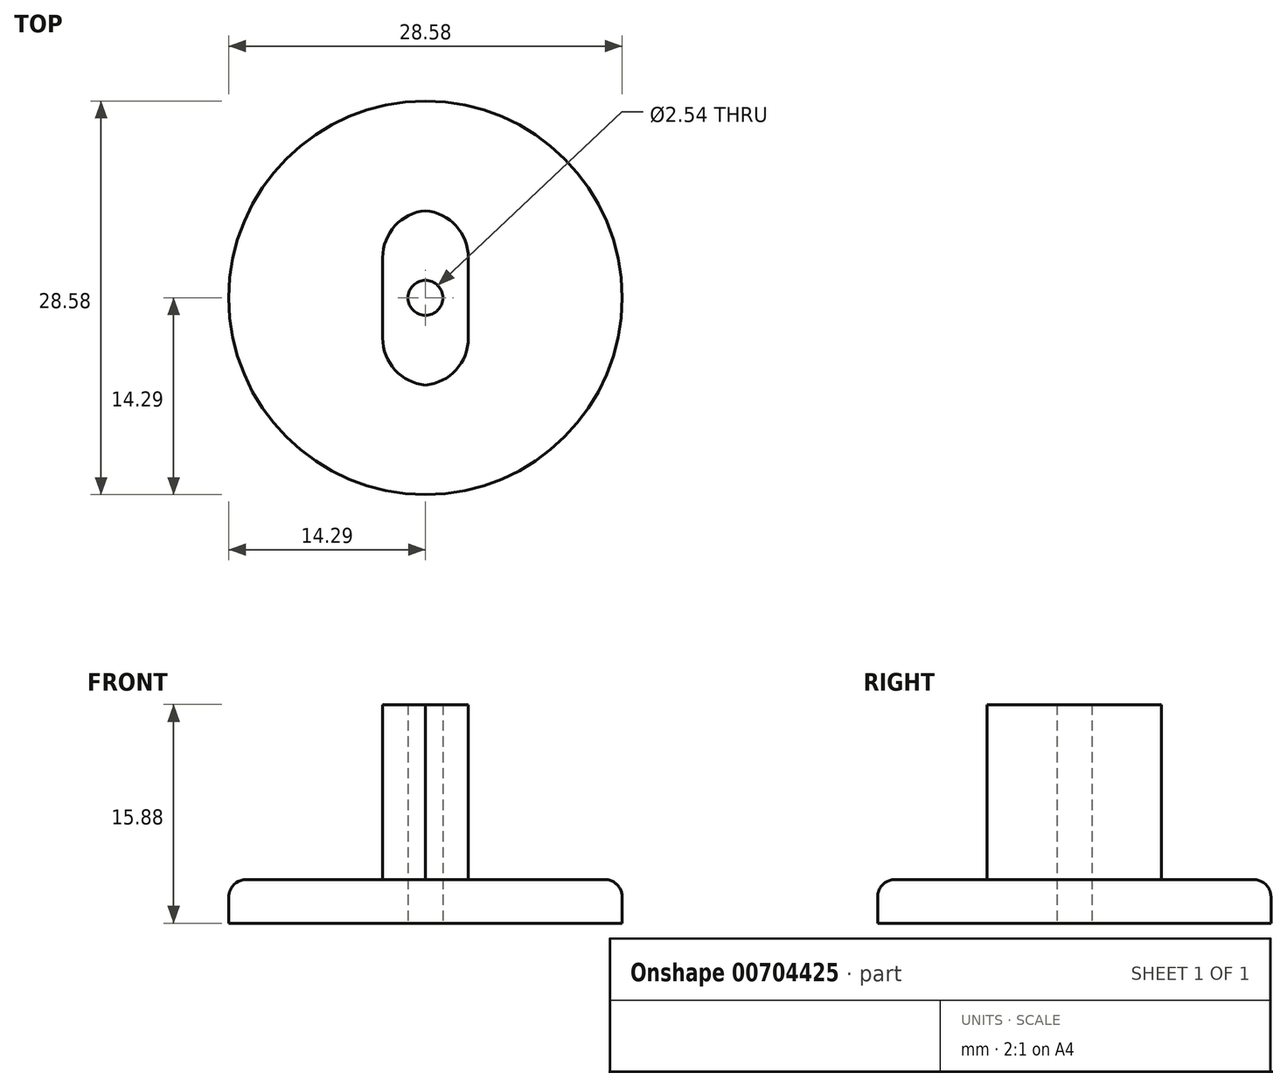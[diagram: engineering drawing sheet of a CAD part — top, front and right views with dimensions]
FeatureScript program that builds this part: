
annotation { "Feature Type Name" : "Feature", "Feature Type Description" : "" }
export const myFeature = defineFeature(function(context is Context, id is Id, definition is map)
    precondition{}
    {
        {
            var Q0;
            Q0=qCreatedBy(makeId("Top.planeOp"),FACE);
            var sketch = newSketch(context, id + "F0", { "sketchPlane" : qUnion([Q0])});
            skCircle(sketch, "E0", {"center": v(0, 0) * mm, "radius": 14.29 * mm});
            skSolve(sketch);
        }
        {
            var Q0;
            Q0 = qSketchRegion(id + "F0", true);
            var Q1;
            Q1 = qSketchRegion(id + "F64pG9NLJwbXjTU_1", true);
            extrude(context, id + "F1", {"entities" : qUnion([Q0, Q1]), "depth" : 3.17 * mm, "offsetDistance" : 25.4 * mm});
        }
        {
            var Q0;
            Q0=makeQuery(id+"F1.opExtrude","CAP_FACE",FACE,{"disambiguationData":[OSD([sQuery(id+"F0.wireOp",EDGE,"E0")])],"isStart":true});
            var sketch = newSketch(context, id + "F2", { "sketchPlane" : qUnion([Q0])});
            skCircle(sketch, "E1", {"center": v(0, 0) * mm, "radius": 0.64 * mm});
            skSolve(sketch);
        }
        {
            var Q0;
            Q0=sQuery(id+"F2.wireOp",VERTEX,"E1.center");
            var Q1;
            Q1=makeQuery(id+"F1.opExtrude","SWEPT_BODY",BODY,{"disambiguationData":[OSD([sQuery(id+"F0.wireOp",EDGE,"E0")])]});
            hole(context, id + "F3", {"style" : HoleStyle.SIMPLE, "endStyle" : HoleEndStyle.THROUGH, "holeDiameter" : 2.54 * mm, "majorDiameter" : 6.35 * mm, "isTappedThrough" : true, "tappedDepth" : 12.7 * mm, "tapClearance" : 3, "locations" : qUnion([Q0]), "scope" : qUnion([Q1])});
        }
        {
            var Q0;
            Q0=makeQuery(id+"F1.opExtrude","CAP_EDGE",EDGE,{"disambiguationData":[OSD([sQuery(id+"F0.wireOp",EDGE,"E0")])],"isStart":false});
            fillet(context, id + "F4", {"entities" : qUnion([Q0]), "radius" : 1.27 * mm, "tangentPropagation" : true, "allowEdgeOverflow" : false});
        }
        {
            var Q0;
            Q0=makeQuery(id+"F1.opExtrude","CAP_FACE",FACE,{"disambiguationData":[OSD([sQuery(id+"F0.wireOp",EDGE,"E0")])],"isStart":false});
            var sketch = newSketch(context, id + "F5", { "sketchPlane" : qUnion([Q0])});
            skLineSegment(sketch, "E2.bottom", {"start": v(3.11, 6.35) * mm, "end": v(-3.11, 6.35) * mm});
            skLineSegment(sketch, "E2.top", {"start": v(3.11, -6.35) * mm, "end": v(-3.11, -6.35) * mm});
            skLineSegment(sketch, "E2.left", {"start": v(3.11, 6.35) * mm, "end": v(3.11, -6.35) * mm});
            skLineSegment(sketch, "E2.right", {"start": v(-3.11, 6.35) * mm, "end": v(-3.11, -6.35) * mm});
            skPoint(sketch, "E2.middle", {"position": v(0, 0) * mm});
            skPoint(sketch, "E3.middle", {"position": v(0.46, -7.8) * mm});
            skSolve(sketch);
        }
        {
            var Q0;
            Q0=makeQuery(id+"F5.imprint","IMPRINT",FACE,{"disambiguationData":[TD([[makeQuery(id+"F5.imprint","IMPRINT",EDGE,{"derivedFrom":sQuery(id+"F5.wireOp",EDGE,"E2.bottom")}),1.0]])]});
            extrude(context, id + "F6", {"entities" : qUnion([Q0]), "operationType" : NewBodyOperationType.ADD, "depth" : 12.7 * mm, "offsetDistance" : 25.4 * mm});
        }
        {
            var Q0;
            Q0=makeQuery(id+"F6.opExtrude","SWEPT_EDGE",EDGE,{"disambiguationData":[OSD([sQuery(id+"F5.wireOp",EDGE,"E2.bottom"),sQuery(id+"F5.wireOp",EDGE,"E2.right")])]});
            var Q1;
            Q1=makeQuery(id+"F6.opExtrude","SWEPT_EDGE",EDGE,{"disambiguationData":[OSD([sQuery(id+"F5.wireOp",EDGE,"E2.top"),sQuery(id+"F5.wireOp",EDGE,"E2.right")])]});
            var Q2;
            Q2=makeQuery(id+"F6.opExtrude","SWEPT_EDGE",EDGE,{"disambiguationData":[OSD([sQuery(id+"F5.wireOp",EDGE,"E2.bottom"),sQuery(id+"F5.wireOp",EDGE,"E2.left")])]});
            var Q3;
            Q3=makeQuery(id+"F6.opExtrude","SWEPT_EDGE",EDGE,{"disambiguationData":[OSD([sQuery(id+"F5.wireOp",EDGE,"E2.top"),sQuery(id+"F5.wireOp",EDGE,"E2.left")])]});
            fillet(context, id + "F7", {"entities" : qUnion([Q0, Q1, Q2, Q3]), "radius" : 3.43 * mm, "tangentPropagation" : true, "allowEdgeOverflow" : false});
        }
    });
